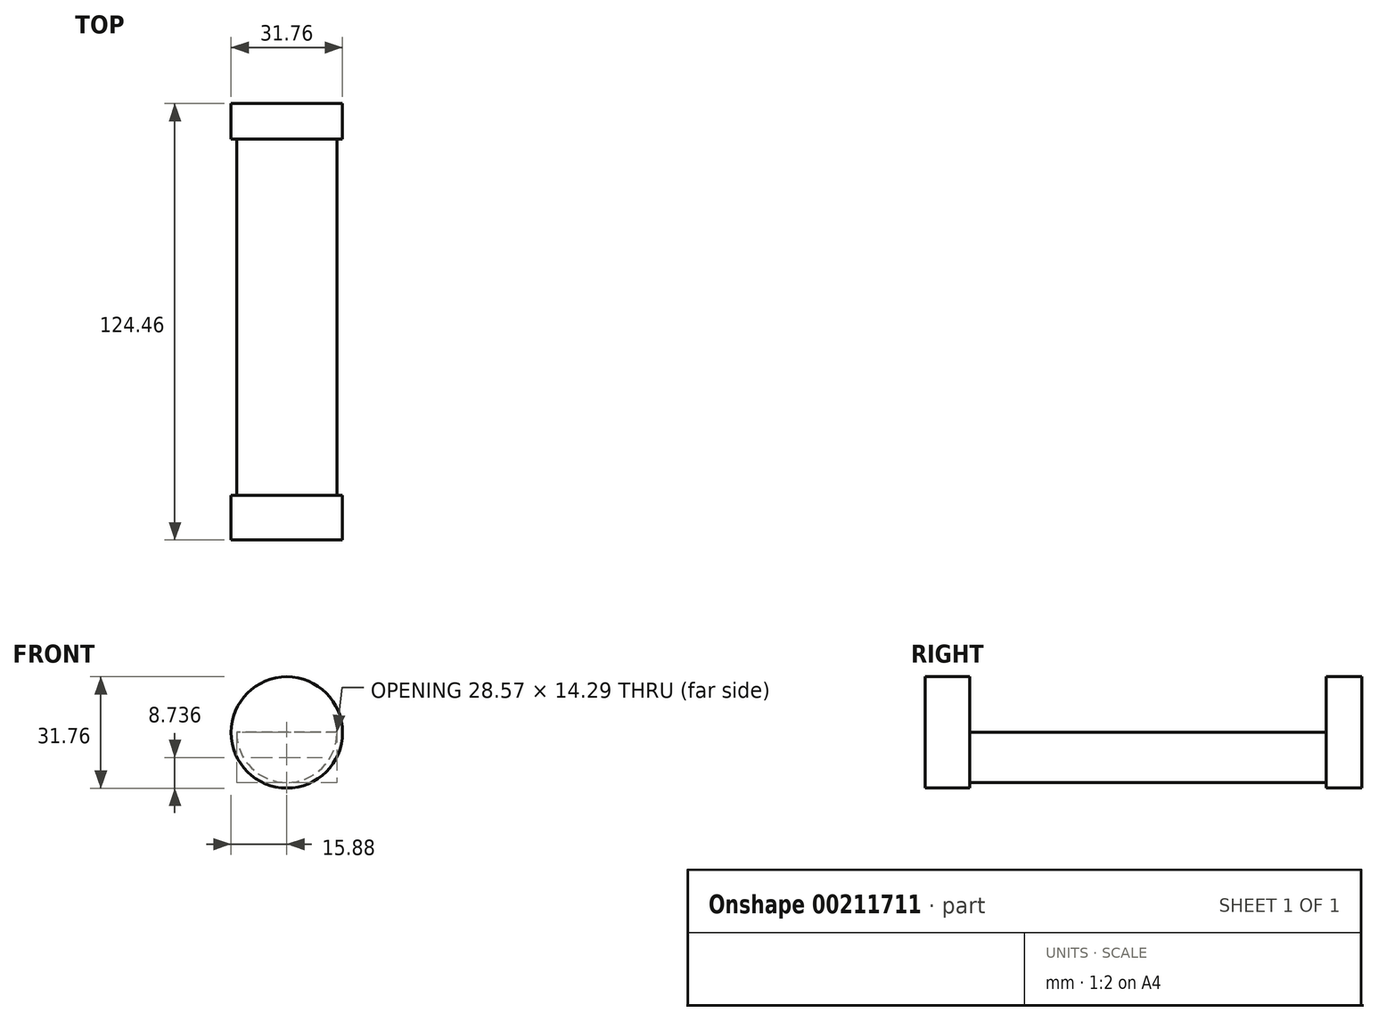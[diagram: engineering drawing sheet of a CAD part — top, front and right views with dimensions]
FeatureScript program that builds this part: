
annotation { "Feature Type Name" : "Feature", "Feature Type Description" : "" }
export const myFeature = defineFeature(function(context is Context, id is Id, definition is map)
    precondition{}
    {
        {
            var Q0;
            Q0=qCreatedBy(makeId("Front.planeOp"),FACE);
            var sketch = newSketch(context, id + "F0", { "sketchPlane" : qUnion([Q0])});
            skCircle(sketch, "E0", {"center": v(0, 0) * mm, "radius": 14.29 * mm});
            skSolve(sketch);
        }
        {
            var Q0;
            Q0 = qSketchRegion(id + "F0", true);
            extrude(context, id + "F1", {"entities" : qUnion([Q0]), "depth" : 101.6 * mm});
        }
        {
            var Q0;
            Q0=makeQuery(id+"F1.opExtrude","CAP_FACE",FACE,{"disambiguationData":[OSD([sQuery(id+"F0.wireOp",EDGE,"E0")])],"isStart":false});
            var sketch = newSketch(context, id + "F2", { "sketchPlane" : qUnion([Q0])});
            skCircle(sketch, "E1", {"center": v(0, 0) * mm, "radius": 15.88 * mm});
            skSolve(sketch);
        }
        {
            var Q0;
            Q0 = qSketchRegion(id + "F2", true);
            extrude(context, id + "F3", {"entities" : qUnion([Q0]), "operationType" : NewBodyOperationType.ADD, "depth" : 12.7 * mm});
        }
        {
            var Q0;
            Q0=makeQuery(id+"F1.opExtrude","CAP_FACE",FACE,{"disambiguationData":[OSD([sQuery(id+"F0.wireOp",EDGE,"E0")])],"isStart":true});
            var sketch = newSketch(context, id + "F4", { "sketchPlane" : qUnion([Q0])});
            skCircle(sketch, "E2", {"center": v(0, 0) * mm, "radius": 15.88 * mm});
            skSolve(sketch);
        }
        {
            var Q0;
            Q0 = qSketchRegion(id + "F4", true);
            extrude(context, id + "F5", {"entities" : qUnion([Q0]), "operationType" : NewBodyOperationType.ADD, "depth" : 10.16 * mm});
        }
        {
            var Q0;
            Q0=qCreatedBy(makeId("Front.planeOp"),FACE);
            var sketch = newSketch(context, id + "F6", { "sketchPlane" : qUnion([Q0])});
            skLineSegment(sketch, "E3", {"start": v(0, 0) * mm, "end": v(14.29, 0) * mm});
            skLineSegment(sketch, "E4", {"start": v(0, 0) * mm, "end": v(-14.29, 0) * mm});
            skArc(sketch, "E5", {"start": v(14.29, 0) * mm, "mid": v(0, 14.29) * mm, "end": v(-14.29, 0) * mm});
            skSolve(sketch);
        }
        {
            var Q0;
            Q0 = qSketchRegion(id + "F6", true);
            extrude(context, id + "F7", {"entities" : qUnion([Q0]), "operationType" : NewBodyOperationType.REMOVE, "depth" : 101.6 * mm});
        }
    });
